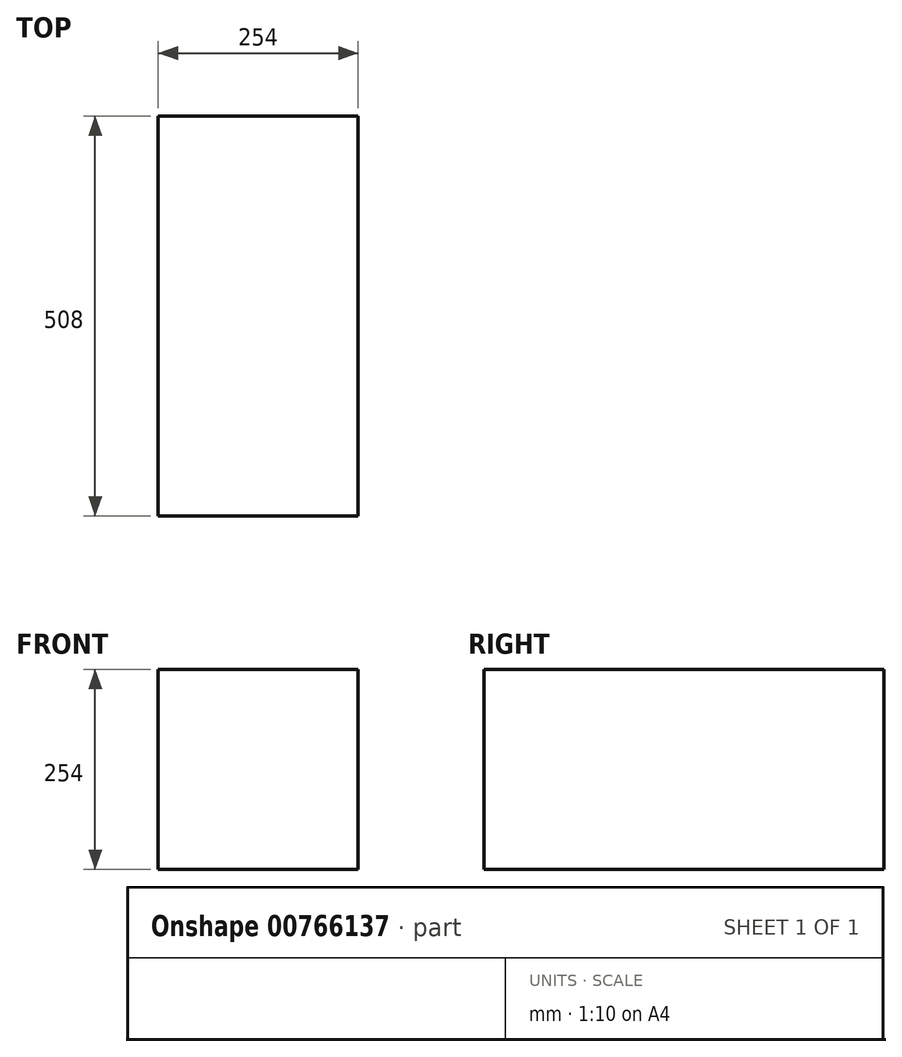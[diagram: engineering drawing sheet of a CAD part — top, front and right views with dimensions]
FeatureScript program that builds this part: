
annotation { "Feature Type Name" : "Feature", "Feature Type Description" : "" }
export const myFeature = defineFeature(function(context is Context, id is Id, definition is map)
    precondition{}
    {
        {
            var Q0;
            Q0=qCreatedBy(makeId("Right.planeOp"),FACE);
            var sketch = newSketch(context, id + "F0", { "sketchPlane" : qUnion([Q0])});
            skLineSegment(sketch, "E0.bottom", {"start": v(0, 0) * mm, "end": v(-508, 0) * mm});
            skLineSegment(sketch, "E0.top", {"start": v(0, -254) * mm, "end": v(-508, -254) * mm});
            skLineSegment(sketch, "E0.left", {"start": v(0, 0) * mm, "end": v(0, -254) * mm});
            skLineSegment(sketch, "E0.right", {"start": v(-508, 0) * mm, "end": v(-508, -254) * mm});
            skSolve(sketch);
        }
        {
            var Q0;
            Q0=makeQuery(id+"F0.imprint","IMPRINT",FACE,{"disambiguationData":[TD([[makeQuery(id+"F0.imprint","IMPRINT",EDGE,{"derivedFrom":sQuery(id+"F0.wireOp",EDGE,"E0.bottom")}),1.0]])]});
            extrude(context, id + "F1", {"entities" : qUnion([Q0]), "depth" : 254 * mm, "offsetDistance" : 25.4 * mm});
        }
    });
